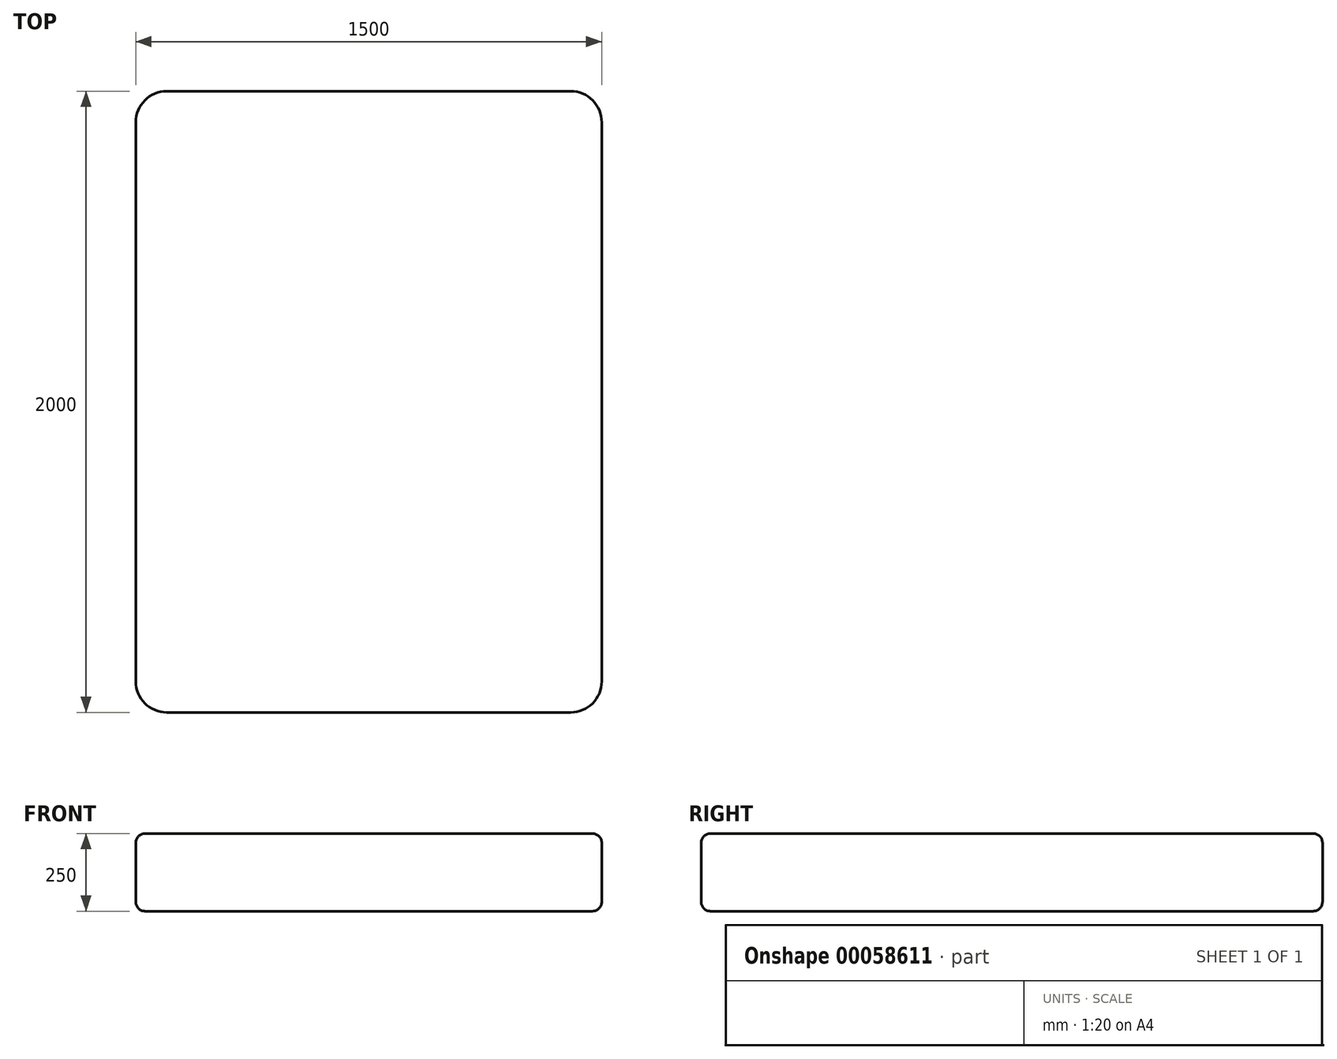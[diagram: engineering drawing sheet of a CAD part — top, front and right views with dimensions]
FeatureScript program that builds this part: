
annotation { "Feature Type Name" : "Feature", "Feature Type Description" : "" }
export const myFeature = defineFeature(function(context is Context, id is Id, definition is map)
    precondition{}
    {
        {
            var Q0;
            Q0=qCreatedBy(makeId("Top.planeOp"),FACE);
            var sketch = newSketch(context, id + "F0", { "sketchPlane" : qUnion([Q0])});
            skLineSegment(sketch, "E0.bottom", {"start": v(100, 0) * mm, "end": v(1400, 0) * mm});
            skLineSegment(sketch, "E0.top", {"start": v(100, 2000) * mm, "end": v(1400, 2000) * mm});
            skLineSegment(sketch, "E0.left", {"start": v(0, 100) * mm, "end": v(0, 1900) * mm});
            skLineSegment(sketch, "E0.right", {"start": v(1500, 100) * mm, "end": v(1500, 1900) * mm});
            skPoint(sketch, "E1.visualSharp", {"position": v(0, 2000) * mm});
            skArc(sketch, "E1.filletArc", {"start": v(100, 2000) * mm, "mid": v(29.29, 1970.71) * mm, "end": v(0, 1900) * mm});
            skPoint(sketch, "E2.visualSharp", {"position": v(1500, 2000) * mm});
            skArc(sketch, "E2.filletArc", {"start": v(1500, 1900) * mm, "mid": v(1470.71, 1970.71) * mm, "end": v(1400, 2000) * mm});
            skPoint(sketch, "E3.visualSharp", {"position": v(1500, 0) * mm});
            skArc(sketch, "E3.filletArc", {"start": v(1400, 0) * mm, "mid": v(1470.71, 29.29) * mm, "end": v(1500, 100) * mm});
            skPoint(sketch, "E4.visualSharp", {"position": v(0, 0) * mm});
            skArc(sketch, "E4.filletArc", {"start": v(0, 100) * mm, "mid": v(29.29, 29.29) * mm, "end": v(100, 0) * mm});
            skSolve(sketch);
        }
        {
            var Q0;
            Q0=makeQuery(id+"F0.imprint","IMPRINT",FACE,{"disambiguationData":[TD([[makeQuery(id+"F0.imprint","IMPRINT",EDGE,{"derivedFrom":sQuery(id+"F0.wireOp",EDGE,"E0.bottom")}),1.0]])]});
            extrude(context, id + "F1", {"entities" : qUnion([Q0]), "depth" : 250 * mm});
        }
        {
            var Q0;
            Q0=makeQuery(id+"F1.opExtrude","CAP_FACE",FACE,{"disambiguationData":[OSD([sQuery(id+"F0.wireOp",EDGE,"E0.bottom"),sQuery(id+"F0.wireOp",EDGE,"E0.top"),sQuery(id+"F0.wireOp",EDGE,"E0.left"),sQuery(id+"F0.wireOp",EDGE,"E0.right"),sQuery(id+"F0.wireOp",EDGE,"E1.filletArc"),sQuery(id+"F0.wireOp",EDGE,"E2.filletArc"),sQuery(id+"F0.wireOp",EDGE,"E3.filletArc"),sQuery(id+"F0.wireOp",EDGE,"E4.filletArc")])],"isStart":false});
            var Q1;
            Q1=makeQuery(id+"F1.opExtrude","CAP_FACE",FACE,{"disambiguationData":[OSD([sQuery(id+"F0.wireOp",EDGE,"E0.bottom"),sQuery(id+"F0.wireOp",EDGE,"E0.top"),sQuery(id+"F0.wireOp",EDGE,"E0.left"),sQuery(id+"F0.wireOp",EDGE,"E0.right"),sQuery(id+"F0.wireOp",EDGE,"E1.filletArc"),sQuery(id+"F0.wireOp",EDGE,"E2.filletArc"),sQuery(id+"F0.wireOp",EDGE,"E3.filletArc"),sQuery(id+"F0.wireOp",EDGE,"E4.filletArc")])],"isStart":true});
            fillet(context, id + "F2", {"entities" : qUnion([Q0, Q1]), "radius" : 30 * mm, "tangentPropagation" : true, "allowEdgeOverflow" : false});
        }
    });
